# Revit family: BIMLIB_Конвектор_НапольныйСЕстественнойКонвекцией_ВКН400_VITRON
name_source: partatom
category: Оборудование
revit_build: Autodesk Revit 2017 (Build: 20190508_0315(x64)
units: mm (PartAtom-declared; Revit-internal decimal feet)

## family parameters
Всегда вертикально = Да
На основе рабочей плоскости = Нет
Общий = Нет
При загрузке вырезать с полостями = Нет
Размер круглого соединителя = Использовать диаметр
Тип детали = Нормальный
Точка расчета площади = Нет

## types (2) — shared parameters
ADSK_URL документации изделия = https://vitron.ru
ADSK_URL страницы изделия = https://vitron.ru
ADSK_Версия Revit = 2017
ADSK_Единица измерения = шт.
ADSK_Завод-изготовитель = Вилма / VITRON
ADSK_Обозначение = ВКН.400.250
ADSK_Размер_Высота = 400 мм
ADSK_Размер_Диаметр = 15 мм
ADSK_Размер_Ширина = 250 мм
BL_BIM library = https://bimlib.pro
URL = https://vitron.ru
VIT_Максимальная рабочая температура теплоносителя = 95 °C
VIT_Рабочее давление теплоносителя = 1600000.0 Па
Высота теплообменника = 100 мм
Изготовитель = Вилма / VITRON
Количество панелей = 4
Коэффициент n = 2.108
Материал_Корпуса = BIMLIB_ОцинкованнаяСталь_VITRON
Материал_Решетка = BIMLIB_Алюминий_VITRON
Описание = Напольные конвекторы отопления "VITRON" с естественной конвекцией - это отопительные приборы, в которых установлен медно-алюминиевый теплообменник. Тепло передается в отапливаемое помещение путём естественной конвекции.
Позволяет преградить поток холодного воздуха от застеклённых фасадов или окон.
Данный конвектор, используется для отопления жилых, общественных и административных зданий, в том числе детских учреждений, выставочных залов, коттеджей и офисов. Может быть установлен как в однотрубную, так и в двухтрубную систему отопления.
Рекомендуется применять только в насосных системах отопления.
Подключение с торца = Подключение с торца
Подключение снизу = Подключение снизу
Расстояние между патрубками = 50 мм
Теплообменник_Горизонтальный = Нет

## per-type parameters (varying)
| type | VIT_Тепловая мощность на 1 м | Количество труб теплообменника | Ширина теплообменника |
| Конвектор_Шириной 250мм_6трубный | 3094.602 Вт | 6 | 150 мм |
| Конвектор_Шириной 250мм_8трубный | 4298.059 Вт | 8 | 200 мм |
